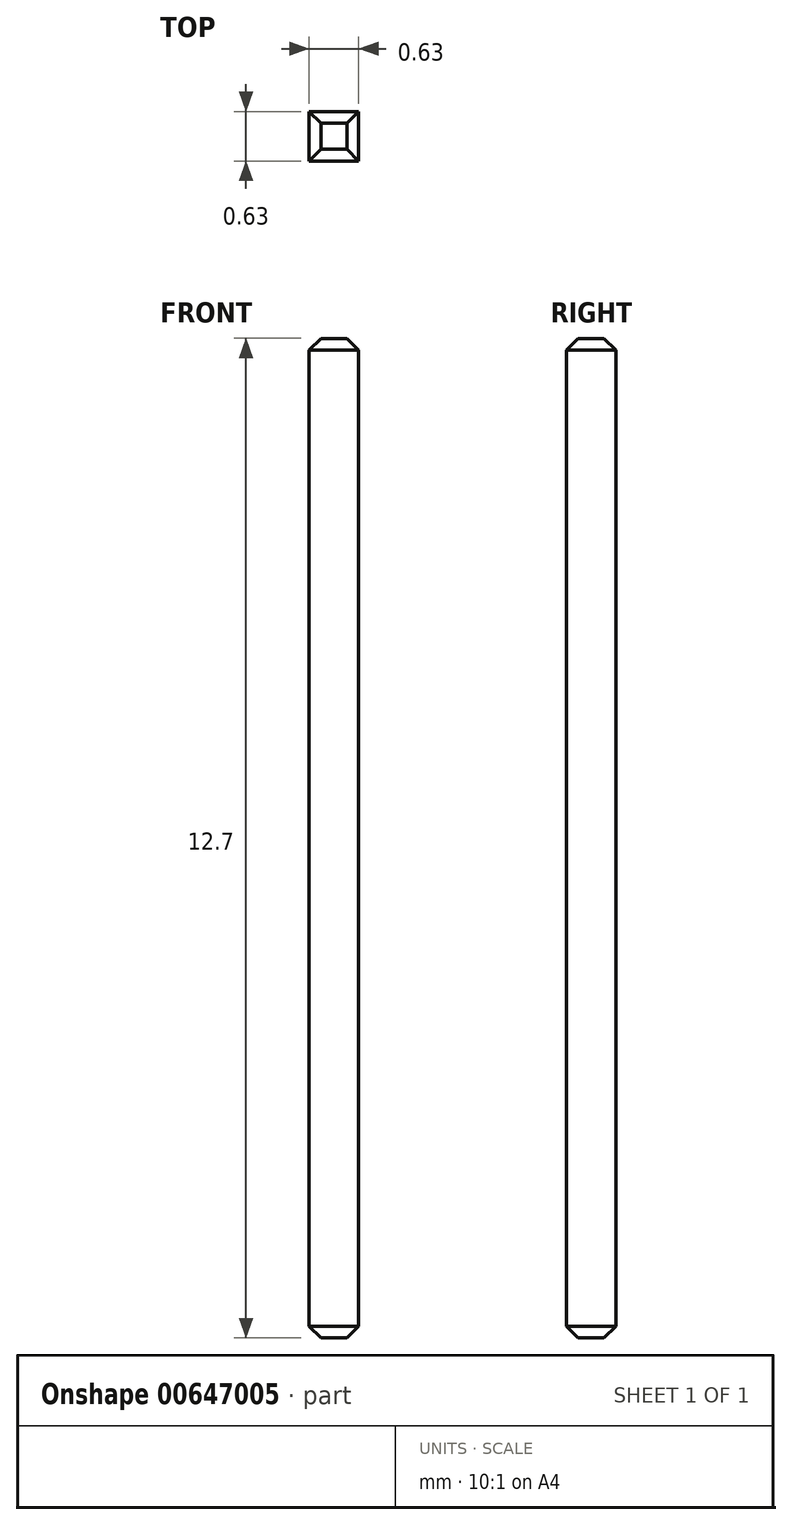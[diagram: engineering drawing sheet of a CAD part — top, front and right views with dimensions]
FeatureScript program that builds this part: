
annotation { "Feature Type Name" : "Feature", "Feature Type Description" : "" }
export const myFeature = defineFeature(function(context is Context, id is Id, definition is map)
    precondition{}
    {
        {
            var Q0;
            Q0=qCreatedBy(makeId("Front.planeOp"),FACE);
            var sketch = newSketch(context, id + "F0", { "sketchPlane" : qUnion([Q0])});
            skLineSegment(sketch, "E0.left", {"start": v(-0.25, 6.35) * mm, "end": v(-0.25, -6.35) * mm});
            skLineSegment(sketch, "E0.right", {"start": v(0.38, 6.35) * mm, "end": v(0.38, -6.35) * mm});
            skPoint(sketch, "E1.endSnap0", {"position": v(0.07, 6.35) * mm});
            skPoint(sketch, "E2.endSnap0", {"position": v(0.07, -6.35) * mm});
            skLineSegment(sketch, "E3", {"start": v(-0.25, -6.35) * mm, "end": v(0.38, -6.35) * mm});
            skLineSegment(sketch, "E4", {"start": v(0.38, 6.35) * mm, "end": v(-0.25, 6.35) * mm});
            skSolve(sketch);
        }
        {
            var Q0;
            Q0 = qSketchRegion(id + "F0", true);
            extrude(context, id + "F1", {"entities" : qUnion([Q0]), "depth" : 0.63 * mm, "offsetDistance" : 25 * mm});
        }
        {
            var Q0;
            Q0=makeQuery(id+"F1.opExtrude","CAP_EDGE",EDGE,{"disambiguationData":[OSD([sQuery(id+"F0.wireOp",EDGE,"E4")])],"isStart":false});
            var Q1;
            Q1=makeQuery(id+"F1.opExtrude","SWEPT_EDGE",EDGE,{"disambiguationData":[OSD([sQuery(id+"F0.wireOp",EDGE,"E0.left"),sQuery(id+"F0.wireOp",EDGE,"E4")])]});
            var Q2;
            Q2=makeQuery(id+"F1.opExtrude","CAP_EDGE",EDGE,{"disambiguationData":[OSD([sQuery(id+"F0.wireOp",EDGE,"E4")])],"isStart":true});
            var Q3;
            Q3=makeQuery(id+"F1.opExtrude","SWEPT_EDGE",EDGE,{"disambiguationData":[OSD([sQuery(id+"F0.wireOp",EDGE,"E0.right"),sQuery(id+"F0.wireOp",EDGE,"E4")])]});
            var Q4;
            Q4=makeQuery(id+"F1.opExtrude","SWEPT_EDGE",EDGE,{"disambiguationData":[OSD([sQuery(id+"F0.wireOp",EDGE,"E0.right"),sQuery(id+"F0.wireOp",EDGE,"E3")])]});
            var Q5;
            Q5=makeQuery(id+"F1.opExtrude","CAP_EDGE",EDGE,{"disambiguationData":[OSD([sQuery(id+"F0.wireOp",EDGE,"E3")])],"isStart":false});
            var Q6;
            Q6=makeQuery(id+"F1.opExtrude","CAP_EDGE",EDGE,{"disambiguationData":[OSD([sQuery(id+"F0.wireOp",EDGE,"E3")])],"isStart":true});
            var Q7;
            Q7=makeQuery(id+"F1.opExtrude","SWEPT_EDGE",EDGE,{"disambiguationData":[OSD([sQuery(id+"F0.wireOp",EDGE,"E0.left"),sQuery(id+"F0.wireOp",EDGE,"E3")])]});
            chamfer(context, id + "F2", {"entities" : qUnion([Q0, Q1, Q2, Q3, Q4, Q5, Q6, Q7]), "width" : 0.15 * mm, "tangentPropagation" : true});
        }
    });
